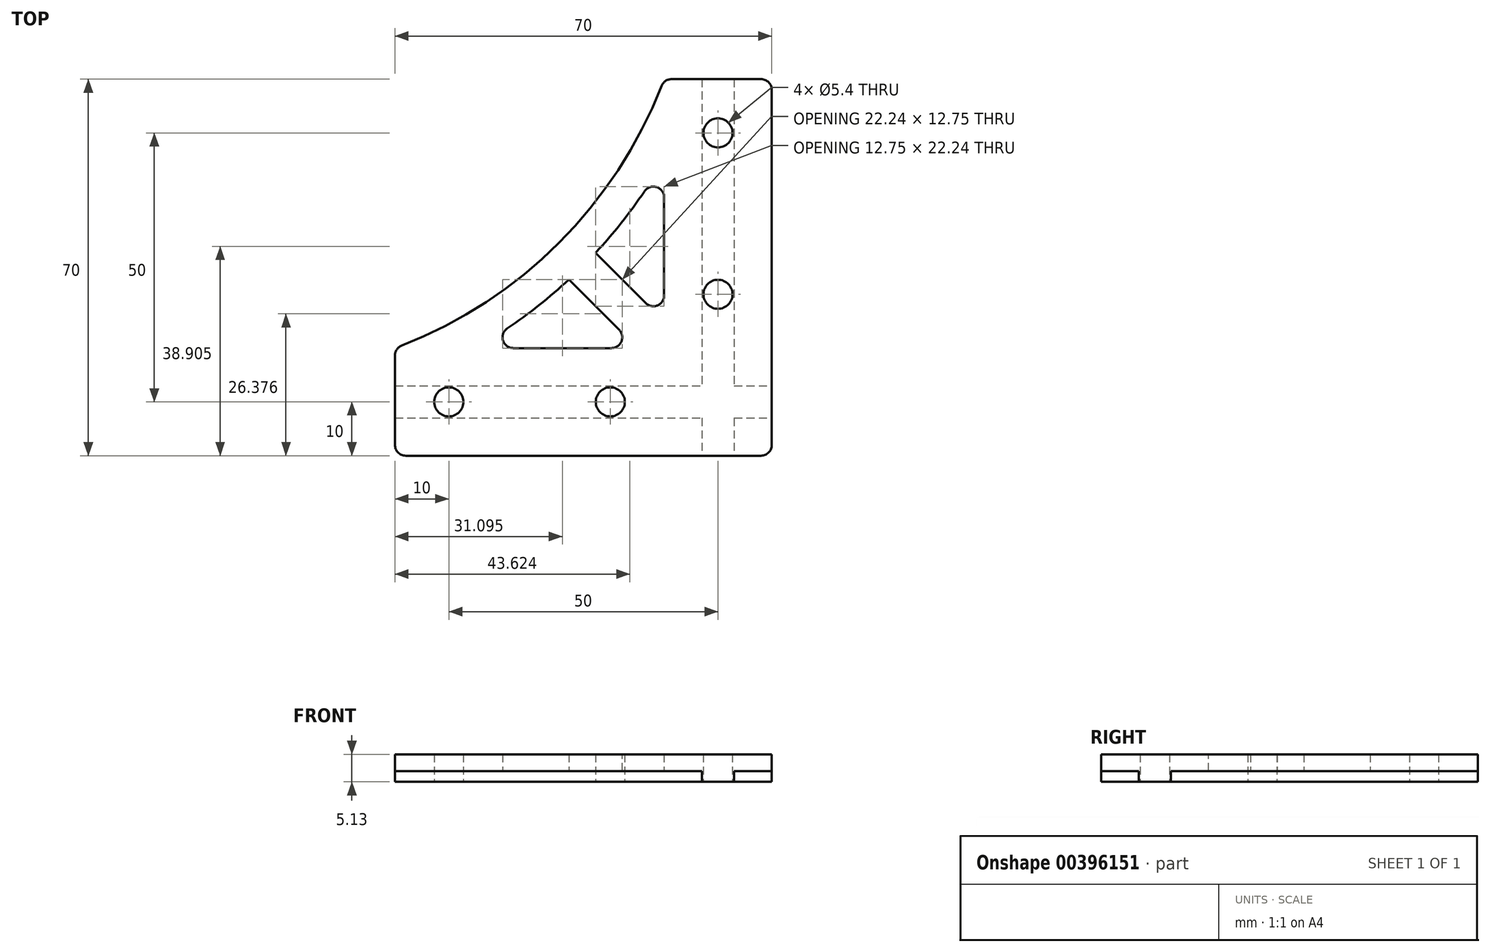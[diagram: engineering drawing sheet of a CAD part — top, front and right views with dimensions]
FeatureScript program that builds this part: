
annotation { "Feature Type Name" : "Feature", "Feature Type Description" : "" }
export const myFeature = defineFeature(function(context is Context, id is Id, definition is map)
    precondition{}
    {
        {
            var Q0;
            Q0=qCreatedBy(makeId("Top.planeOp"),FACE);
            var sketch = newSketch(context, id + "F0", { "sketchPlane" : qUnion([Q0])});
            skLineSegment(sketch, "E0.bottom", {"start": v(-35, 35) * mm, "end": v(35, 35) * mm});
            skLineSegment(sketch, "E0.top", {"start": v(-35, -35) * mm, "end": v(35, -35) * mm});
            skLineSegment(sketch, "E0.left", {"start": v(-35, 35) * mm, "end": v(-35, -35) * mm});
            skLineSegment(sketch, "E0.right", {"start": v(35, 35) * mm, "end": v(35, -35) * mm});
            skPoint(sketch, "E0.middle", {"position": v(0, 0) * mm});
            skLineSegment(sketch, "E1", {"start": v(15, 35) * mm, "end": v(-35, -15) * mm});
            skArc(sketch, "E2", {"start": v(-35, -15) * mm, "mid": v(-4.55, 4.55) * mm, "end": v(15, 35) * mm});
            skSolve(sketch);
        }
        {
            var Q0;
            {var subQ2=sQuery(id+"F0.wireOp",EDGE,"E0.top");Q0=makeQuery(id+"F0.imprint","IMPRINT",FACE,{"disambiguationData":[TD([[makeQuery(id+"F0.imprint","IMPRINT",EDGE,{"derivedFrom":subQ2}),1.0]])]});}
            var Q1;
            {var subQ0=sQuery(id+"F0.wireOp",EDGE,"E0.right");var subQ1=sQuery(id+"F0.wireOp",EDGE,"E0.bottom");var subQ2=makeQuery(id+"F0.imprint","INTERSECT",VERTEX,{"derivedFrom":[subQ1,subQ0]});Q1=makeQuery(id+"F0.imprint","IMPRINT",FACE,{"disambiguationData":[TD([[makeQuery(id+"F0.imprint","IMPRINT",EDGE,{"disambiguationData":[TD([[subQ2,-1.0]])],"derivedFrom":subQ0}),-1.0]])]});}
            var Q2;
            {var subQ1=sQuery(id+"F0.wireOp",EDGE,"E0.right");var subQ5=sQuery(id+"F0.wireOp",EDGE,"E0.top");var subQ6=makeQuery(id+"F0.imprint","INTERSECT",VERTEX,{"derivedFrom":[subQ5,subQ1]});Q2=makeQuery(id+"F0.imprint","IMPRINT",FACE,{"disambiguationData":[TD([[makeQuery(id+"F0.imprint","IMPRINT",EDGE,{"disambiguationData":[TD([[subQ6,1.0]])],"derivedFrom":subQ5}),1.0]])]});}
            extrude(context, id + "F1", {"entities" : qUnion([Q0, Q1, Q2]), "depth" : 3.12 * mm});
        }
        {
            var Q0;
            Q0=makeQuery(id+"F1.opExtrude","CAP_FACE",FACE,{"disambiguationData":[OSD([sQuery(id+"F0.wireOp",EDGE,"E0.bottom"),sQuery(id+"F0.wireOp",EDGE,"E0.top"),sQuery(id+"F0.wireOp",EDGE,"E0.left"),sQuery(id+"F0.wireOp",EDGE,"E0.right"),sQuery(id+"F0.wireOp",EDGE,"E1")])],"isStart":true});
            var sketch = newSketch(context, id + "F2", { "sketchPlane" : qUnion([Q0])});
            skLineSegment(sketch, "E3", {"start": v(25, -35) * mm, "end": v(25, 35) * mm, "construction": true});
            skLineSegment(sketch, "E4", {"start": v(-35, 25) * mm, "end": v(35, 25) * mm, "construction": true});
            skLineSegment(sketch, "E5.bottom", {"start": v(22, -35) * mm, "end": v(28, -35) * mm});
            skLineSegment(sketch, "E5.top", {"start": v(22, 35) * mm, "end": v(28, 35) * mm});
            skLineSegment(sketch, "E5.left", {"start": v(22, -35) * mm, "end": v(22, 35) * mm});
            skLineSegment(sketch, "E5.right", {"start": v(28, -35) * mm, "end": v(28, 35) * mm});
            skPoint(sketch, "E5.middle", {"position": v(25, 0) * mm});
            skLineSegment(sketch, "E6.bottom", {"start": v(-35, 22) * mm, "end": v(35, 22) * mm});
            skLineSegment(sketch, "E6.top", {"start": v(-35, 28) * mm, "end": v(35, 28) * mm});
            skLineSegment(sketch, "E6.left", {"start": v(-35, 22) * mm, "end": v(-35, 28) * mm});
            skLineSegment(sketch, "E6.right", {"start": v(35, 22) * mm, "end": v(35, 28) * mm});
            skPoint(sketch, "E6.middle", {"position": v(0, 25) * mm});
            skLineSegment(sketch, "E7.bottom", {"start": v(22, 22) * mm, "end": v(15, 22) * mm});
            skLineSegment(sketch, "E7.top", {"start": v(22, 28) * mm, "end": v(15, 28) * mm});
            skLineSegment(sketch, "E7.left", {"start": v(22, 22) * mm, "end": v(22, 28) * mm});
            skLineSegment(sketch, "E7.right", {"start": v(15, 22) * mm, "end": v(15, 28) * mm});
            skLineSegment(sketch, "E8.bottom", {"start": v(28, 22) * mm, "end": v(22, 22) * mm});
            skLineSegment(sketch, "E8.top", {"start": v(28, 15) * mm, "end": v(22, 15) * mm});
            skLineSegment(sketch, "E8.left", {"start": v(28, 22) * mm, "end": v(28, 15) * mm});
            skLineSegment(sketch, "E8.right", {"start": v(22, 22) * mm, "end": v(22, 15) * mm});
            skSolve(sketch);
        }
        {
            var Q0;
            {var subQ0=sQuery(id+"F2.wireOp",EDGE,"E5.bottom");Q0=makeQuery(id+"F2.imprint","IMPRINT",FACE,{"disambiguationData":[TD([[makeQuery(id+"F2.imprint","IMPRINT",EDGE,{"derivedFrom":subQ0}),1.0]])]});}
            var Q1;
            {var subQ0=sQuery(id+"F2.wireOp",EDGE,"E6.left");Q1=makeQuery(id+"F2.imprint","IMPRINT",FACE,{"disambiguationData":[TD([[makeQuery(id+"F2.imprint","IMPRINT",EDGE,{"derivedFrom":subQ0}),-1.0]])]});}
            var Q2;
            {var subQ0=sQuery(id+"F2.wireOp",EDGE,"E8.top");Q2=makeQuery(id+"F2.imprint","IMPRINT",FACE,{"disambiguationData":[TD([[makeQuery(id+"F2.imprint","IMPRINT",EDGE,{"derivedFrom":subQ0}),1.0]])]});}
            var Q3;
            {var subQ0=sQuery(id+"F2.wireOp",EDGE,"d9nGMlHh-qkIi-XzYH-rveG-kUuO3HYsBL67");var subQ1=sQuery(id+"F2.wireOp",EDGE,"E5.left");var subQ2=makeQuery(id+"F2.imprint","INTERSECT",VERTEX,{"derivedFrom":[subQ1,subQ0]});Q3=makeQuery(id+"F2.imprint","IMPRINT",FACE,{"disambiguationData":[TD([[makeQuery(id+"F2.imprint","IMPRINT",EDGE,{"disambiguationData":[TD([[subQ2,-1.0]])],"derivedFrom":subQ1}),-1.0]])]});}
            var Q4;
            {var subQ0=sQuery(id+"F2.wireOp",EDGE,"E7.right");Q4=makeQuery(id+"F2.imprint","IMPRINT",FACE,{"disambiguationData":[TD([[makeQuery(id+"F2.imprint","IMPRINT",EDGE,{"derivedFrom":subQ0}),1.0]])]});}
            var Q5;
            {var subQ0=sQuery(id+"F2.wireOp",EDGE,"Tg9qOg1b-ZZ8D-OlWz-hFwT-lKIjL2JHWv4c");var subQ1=sQuery(id+"F2.wireOp",EDGE,"E6.bottom");var subQ2=makeQuery(id+"F2.imprint","INTERSECT",VERTEX,{"derivedFrom":[subQ1,subQ0]});Q5=makeQuery(id+"F2.imprint","IMPRINT",FACE,{"disambiguationData":[TD([[makeQuery(id+"F2.imprint","IMPRINT",EDGE,{"disambiguationData":[TD([[subQ2,-1.0]])],"derivedFrom":subQ1}),1.0]])]});}
            extrude(context, id + "F3", {"entities" : qUnion([Q0, Q1, Q2, Q3, Q4, Q5]), "operationType" : NewBodyOperationType.ADD, "depth" : 2 * mm});
        }
        {
            var Q0;
            Q0=makeQuery(id+"F3.opExtrude","CAP_FACE",FACE,{"disambiguationData":[OSD([sQuery(id+"F2.wireOp",EDGE,"E5.bottom"),sQuery(id+"F2.wireOp",EDGE,"E5.left"),sQuery(id+"F2.wireOp",EDGE,"E5.right"),sQuery(id+"F2.wireOp",EDGE,"E8.top")])],"isStart":false});
            var sketch = newSketch(context, id + "F4", { "sketchPlane" : qUnion([Q0])});
            skCircle(sketch, "E9", {"center": v(25, -25) * mm, "radius": 2.7 * mm});
            skCircle(sketch, "E10", {"center": v(25, 5) * mm, "radius": 2.7 * mm});
            skCircle(sketch, "E11", {"center": v(5, 25) * mm, "radius": 2.7 * mm});
            skCircle(sketch, "E12", {"center": v(-25, 25) * mm, "radius": 2.7 * mm});
            skSolve(sketch);
        }
        {
            var Q0;
            Q0=makeQuery(id+"F4.imprint","IMPRINT",FACE,{"disambiguationData":[TD([[makeQuery(id+"F4.imprint","IMPRINT",EDGE,{"derivedFrom":sQuery(id+"F4.wireOp",EDGE,"E9")}),1.0]])]});
            var Q1;
            Q1=makeQuery(id+"F4.imprint","IMPRINT",FACE,{"disambiguationData":[TD([[makeQuery(id+"F4.imprint","IMPRINT",EDGE,{"derivedFrom":sQuery(id+"F4.wireOp",EDGE,"E10")}),1.0]])]});
            var Q2;
            Q2=makeQuery(id+"F4.imprint","IMPRINT",FACE,{"disambiguationData":[TD([[makeQuery(id+"F4.imprint","IMPRINT",EDGE,{"derivedFrom":sQuery(id+"F4.wireOp",EDGE,"E11")}),1.0]])]});
            var Q3;
            Q3=makeQuery(id+"F4.imprint","IMPRINT",FACE,{"disambiguationData":[TD([[makeQuery(id+"F4.imprint","IMPRINT",EDGE,{"derivedFrom":sQuery(id+"F4.wireOp",EDGE,"E12")}),1.0]])]});
            extrude(context, id + "F5", {"entities" : qUnion([Q0, Q1, Q2, Q3]), "operationType" : NewBodyOperationType.REMOVE, "oppositeDirection" : true, "depth" : 25 * mm});
        }
        {
            var Q0;
            Q0=makeQuery(id+"F1.opExtrude","SWEPT_EDGE",EDGE,{"disambiguationData":[OSD([sQuery(id+"F0.wireOp",EDGE,"E0.bottom"),sQuery(id+"F0.wireOp",EDGE,"E0.right")])]});
            var Q1;
            Q1=makeQuery(id+"F1.opExtrude","SWEPT_EDGE",EDGE,{"disambiguationData":[OSD([sQuery(id+"F0.wireOp",EDGE,"E0.bottom"),sQuery(id+"F0.wireOp",EDGE,"E1")])]});
            var Q2;
            Q2=makeQuery(id+"F1.opExtrude","SWEPT_EDGE",EDGE,{"disambiguationData":[OSD([sQuery(id+"F0.wireOp",EDGE,"E0.left"),sQuery(id+"F0.wireOp",EDGE,"E1")])]});
            var Q3;
            Q3=makeQuery(id+"F1.opExtrude","SWEPT_EDGE",EDGE,{"disambiguationData":[OSD([sQuery(id+"F0.wireOp",EDGE,"E0.top"),sQuery(id+"F0.wireOp",EDGE,"E0.left")])]});
            var Q4;
            Q4=makeQuery(id+"F1.opExtrude","SWEPT_EDGE",EDGE,{"disambiguationData":[OSD([sQuery(id+"F0.wireOp",EDGE,"E0.top"),sQuery(id+"F0.wireOp",EDGE,"E0.right")])]});
            fillet(context, id + "F6", {"entities" : qUnion([Q0, Q1, Q2, Q3, Q4]), "radius" : 2 * mm, "tangentPropagation" : true, "allowEdgeOverflow" : false});
        }
        {
            var Q0;
            Q0=qCreatedBy(makeId("Top.planeOp"),FACE);
            var sketch = newSketch(context, id + "F7", { "sketchPlane" : qUnion([Q0])});
            skLineSegment(sketch, "E13.bottom", {"start": v(15, 20) * mm, "end": v(-20, 20) * mm});
            skLineSegment(sketch, "E13.top", {"start": v(15, -15) * mm, "end": v(-20, -15) * mm});
            skLineSegment(sketch, "E13.left", {"start": v(15, 20) * mm, "end": v(15, -15) * mm});
            skLineSegment(sketch, "E13.right", {"start": v(-20, 20) * mm, "end": v(-20, -15) * mm});
            skLineSegment(sketch, "E14", {"start": v(15, 20) * mm, "end": v(-20, -15) * mm});
            skArc(sketch, "E15", {"start": v(-20, -15) * mm, "mid": v(-0.18, 0.18) * mm, "end": v(15, 20) * mm});
            skLineSegment(sketch, "E16", {"start": v(0, 0) * mm, "end": v(36.97, -36.97) * mm, "construction": true});
            skLineSegment(sketch, "E17", {"start": v(-0.03, 4.97) * mm, "end": v(42.01, -37.06) * mm});
            skLineSegment(sketch, "E18", {"start": v(-4.97, 0.03) * mm, "end": v(36.42, -41.37) * mm});
            skSolve(sketch);
        }
        {
            var Q0;
            Q0=makeQuery(id+"F7.imprint","IMPRINT",FACE,{"disambiguationData":[TD([[makeQuery(id+"F7.imprint","IMPRINT",EDGE,{"derivedFrom":sQuery(id+"F7.wireOp",EDGE,"E13.top")}),-1.0]])]});
            var Q1;
            {var subQ1=sQuery(id+"F7.wireOp",EDGE,"E13.left");var subQ3=sQuery(id+"F7.wireOp",EDGE,"E17");var subQ4=makeQuery(id+"F7.imprint","INTERSECT",VERTEX,{"derivedFrom":[subQ1,subQ3]});Q1=makeQuery(id+"F7.imprint","IMPRINT",FACE,{"disambiguationData":[TD([[makeQuery(id+"F7.imprint","IMPRINT",EDGE,{"disambiguationData":[TD([[subQ4,1.0]])],"derivedFrom":subQ3}),1.0]])]});}
            extrude(context, id + "F8", {"entities" : qUnion([Q0, Q1]), "operationType" : NewBodyOperationType.REMOVE, "depth" : 25 * mm});
        }
        {
            var Q0;
            Q0=makeQuery(id+"F8.boolean.opBoolean","COPY",EDGE,{"derivedFrom":makeQuery(id+"F8.opExtrude","SWEPT_EDGE",EDGE,{"disambiguationData":[OSD([sQuery(id+"F7.wireOp",EDGE,"E13.bottom"),sQuery(id+"F7.wireOp",EDGE,"E13.left"),sQuery(id+"F7.wireOp",EDGE,"E14")])]})});
            var Q1;
            Q1=makeQuery(id+"F8.boolean.opBoolean","COPY",EDGE,{"derivedFrom":makeQuery(id+"F8.opExtrude","SWEPT_EDGE",EDGE,{"disambiguationData":[OSD([sQuery(id+"F7.wireOp",EDGE,"E13.top"),sQuery(id+"F7.wireOp",EDGE,"E13.left")])]})});
            var Q2;
            Q2=makeQuery(id+"F8.boolean.opBoolean","COPY",EDGE,{"derivedFrom":makeQuery(id+"F8.opExtrude","SWEPT_EDGE",EDGE,{"disambiguationData":[OSD([sQuery(id+"F7.wireOp",EDGE,"E13.top"),sQuery(id+"F7.wireOp",EDGE,"E13.right"),sQuery(id+"F7.wireOp",EDGE,"E14")])]})});
            fillet(context, id + "F9", {"entities" : qUnion([Q0, Q1, Q2]), "radius" : 2 * mm, "tangentPropagation" : true, "allowEdgeOverflow" : false});
        }
    });
